# Revit family: QF_ELECTROLUXPROFESSIONAL_1LSNBN_IC64832LF_G
name_source: partatom
category: Attrezzature speciali
units: mm (PartAtom-declared; Revit-internal decimal feet)

## family parameters
Basato su piano di lavoro = No
Condiviso = No
Punto di calcolo locali = No
Quota connettore circolare = Usa diametro
Sempre verticale = Sì
Taglio con vuoti quando caricato = No
Tipo di parte = Normale

## types (18) — shared parameters
Depth Actual = 1110 mm
Gas KW = 65
Height Actual = 1270 mm  [stored 4.16667 ft]
Latent Heat Output = 0.0
Length Actual = 3835 mm
Modello = IC64832LF
Phase = 3
Produttore = Electrolux Professional
Sensible Heat Output = 0.0
URL = www.electroluxprofessional.com
Weight = 1015
zero-valued in all types: Prospetto di default, Steam Pounds per Hour

## per-type parameters (varying)
| type | Cycle | Descrizione | Item Number | Volts | Watts |
| 9882030134 | 50 Hz | IRONER CYLINDER IC64832LF LENGTH FOLDING 3170MM ACTIVE GAS CE 400/50/3 6MM SST CYL. ML FEED NOW | 1L0GN1 | 400 V | 3200 W |
| 9882030266 | 60 Hz | IRONER CYLINDER IC64832LF LENGTH FOLDING 3170MM ACTIVE GAS CE 208-240/60/3 6MM SST CYL. EN, ES, PO FEED NOW | 1L0H2Z | 240 V | 2000 W |
| 9882030077 | 50 Hz | IRONER CYLINDER IC64832LF LENGTH FOLDING 3170MM SUPERIOR GAS CE 400/50/3 DUBIXIUM FR FEED ALONE VAC.FEED.TABLE ANTISTATI | 1LA1C6 | 400 V | 3200 W |
| 9882030017 | 50 Hz | IRONER CYLINDER IC64832LF LENGTH FOLDING 3170MM GAS CE 400/50/3 DUBIXIUM FR DIAMMS | 1LSNZ3 | 400 V | 3200 W |
| 9882030135 | 50 Hz | IRONER CYLINDER IC64832LF LENGTH FOLDING 3170MM PERFORMANCE GAS CE 400/50/3 DUBIXIUM ML VAC.FEED.TABLE DIAMMS | 1L0GN2 | 400 V | 3200 W |
| 9882030113 | 50 Hz | IRONER CYLINDER IC64832LF LENGTH FOLDING 3170MM GAS CE 400/50/3 DUBIXIUM FR FEED ALONE VAC.FEED.TABLE DIAMMS | 1L999E | 400 V | 3200 W |
| 9882030015 | 50 Hz | IRONER CYLINDER IC64832LF LENGTH FOLDING 3170MM PERFORMANCE GAS CE 400/50/3 DUBIXIUM FR VAC.FEED.TABLE DIAMMS | 1LSNY1 | 400 V | 3200 W |
| 9882030063 | 60 Hz | IRONER CYLINDER IC64832LF LENGTH FOLDING 3170MM GAS CE 208-240/60/3 6MM SST CYL. ML FEED NOW DIAMMS | 1L0GJT | 240 V | 2000 W |
| 9882030243 | 50 Hz | IRONER CYLINDER IC64832LF LENGTH FOLDING 3170MM GAS CE 400/50/3 6MM SST CYL. FR FEED NOW FEED ALONE VAC.FEED.TABLE | 1L0GX8 | 400 V | 3200 W |
| 9882030035 | 50 Hz | IRONER CYLINDER IC64832LF LENGTH FOLDING 3170MM GAS CE 400/50/3 6MM SST CYL. FR FEED NOW FEED ALONE VAC.FEED.TABLE ANTIS | 1LSP01 | 400 V | 3200 W |
| 9882030036 | 50 Hz | IRONER CYLINDER IC64832LF LENGTH FOLDING 3170MM SUPERIOR GAS CE 400/50/3 DUBIXIUM ML FEED ALONE VAC.FEED.TABLE ANTISTATI | 1LSP02 | 400 V | 3200 W |
| 9882030118 | 50 Hz | IRONER CYLINDER IC64832LF LENGTH FOLDING 3170MM ACTIVE GAS CE 400/50/3 6MM SST CYL. FR FEED NOW | 1L0GMJ | 400 V | 3200 W |
| 9882030014 | 50 Hz | IRONER CYLINDER IC64832LF LENGTH FOLDING 3170MM GAS CE 400/50/3 DUBIXIUM ML ANTISTATIC DIAMMS | 1LSNXS | 400 V | 3200 W |
| 9882030001 | 50 Hz | IRONER CYLINDER IC64832LF LENGTH FOLDING 3170MM GAS CE 400/50/3 6MM SST CYL. FR FEED NOW FEED ALONE VAC.FEED.TABLE ANTIS | 1LSNYR | 400 V | 3200 W |
| 9882030012 | 50 Hz | IRONER CYLINDER IC64832LF LENGTH FOLDING 3170MM GAS CE 400/50/3 DUBIXIUM FR ANTISTATIC DIAMMS | 1LSNX7 | 400 V | 3200 W |
| 9882030215 | 50 Hz | IRONER CYLINDER IC64832LF LENGTH FOLDING 3170MM GAS CE 400/50/3 6MM SST CYL. ML DIAMMS | 1L0GTY | 400 V | 3200 W |
| 9882030084 | 50 Hz | IRONER CYLINDER IC64832LF LENGTH FOLDING 3170MM GAS CE 400/50/3 DUBIXIUM FR VAC.FEED.TABLE ANTISTATIC DIAMMS | 1L0GFM | 400 V | 3200 W |
| 9882030049 | 60 Hz | IRONER CYLINDER IC64832LF LENGTH FOLDING 3170MM GAS CE 208-240/60/3 6MM SST CYL. EN, ES, PO ANTISTATIC DIAMMS | 1L821G | 240 V | 2000 W |

note: [stored X ft] marks values corroborated as IEEE doubles in the binary element streams (Revit-internal decimal feet)

## geometry (parser evidence)
native form markers: Sweep x11
no freeform markers — native parametric forms only
